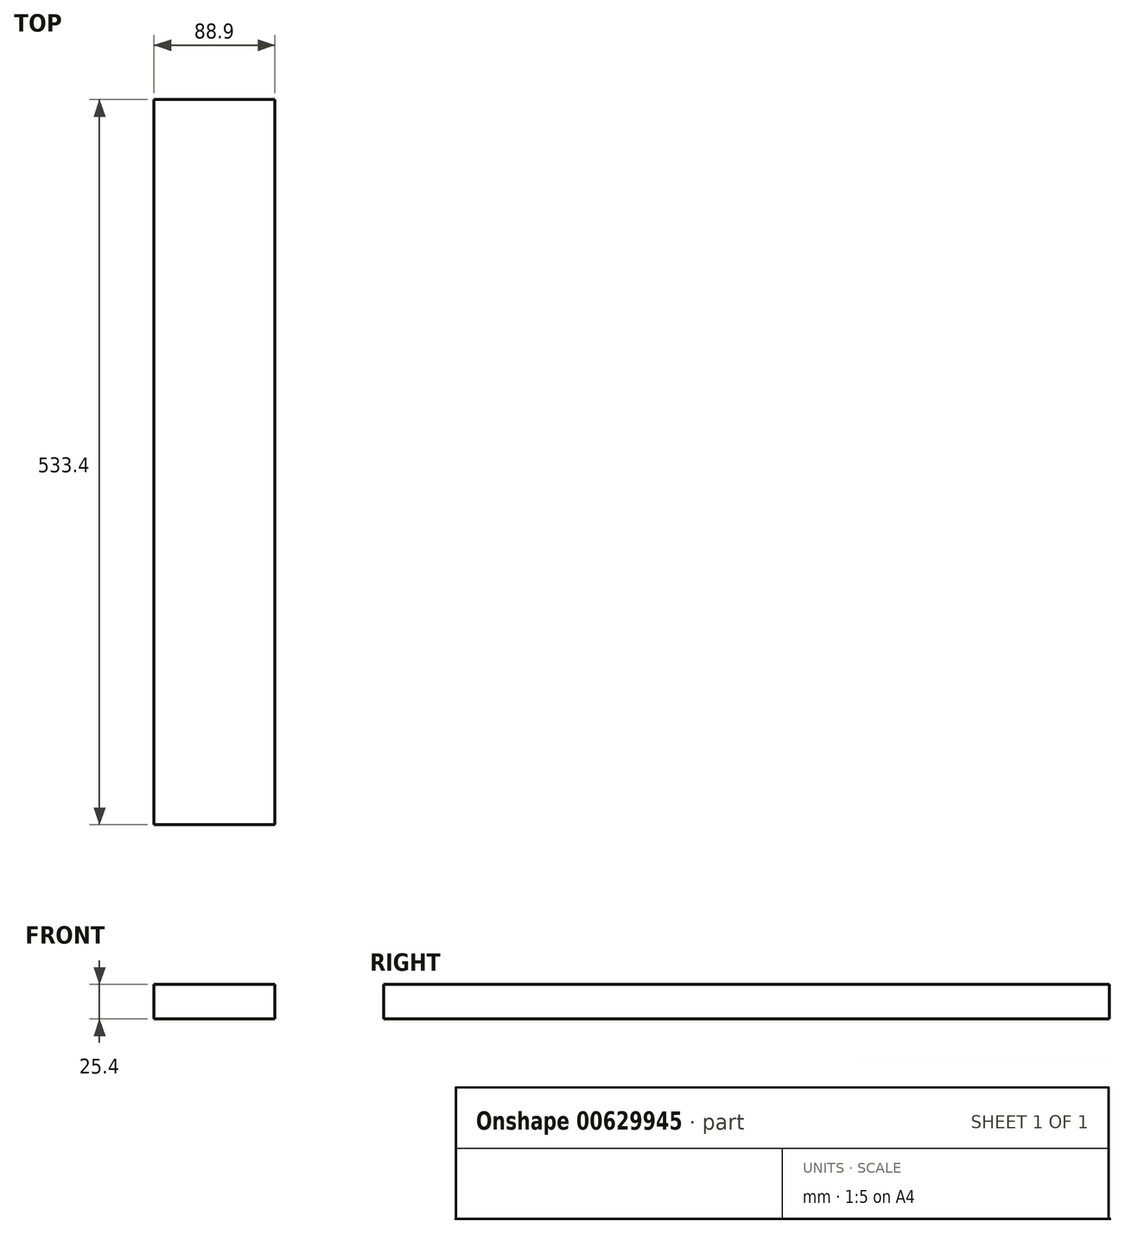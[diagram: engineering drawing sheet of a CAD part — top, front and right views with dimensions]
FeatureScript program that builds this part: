
annotation { "Feature Type Name" : "Feature", "Feature Type Description" : "" }
export const myFeature = defineFeature(function(context is Context, id is Id, definition is map)
    precondition{}
    {
        {
            var Q0;
            Q0=qCreatedBy(makeId("Front.planeOp"),FACE);
            var sketch = newSketch(context, id + "F0", { "sketchPlane" : qUnion([Q0])});
            skLineSegment(sketch, "E0.bottom", {"start": v(-38.14, 25.4) * mm, "end": v(50.76, 25.4) * mm});
            skLineSegment(sketch, "E0.top", {"start": v(-38.14, 0) * mm, "end": v(50.76, 0) * mm});
            skLineSegment(sketch, "E0.left", {"start": v(-38.14, 25.4) * mm, "end": v(-38.14, 0) * mm});
            skLineSegment(sketch, "E0.right", {"start": v(50.76, 25.4) * mm, "end": v(50.76, 0) * mm});
            skSolve(sketch);
        }
        {
            var Q0;
            Q0 = qSketchRegion(id + "F0", true);
            extrude(context, id + "F1", {"entities" : qUnion([Q0]), "depth" : 533.4 * mm, "offsetDistance" : 25.4 * mm});
        }
    });
